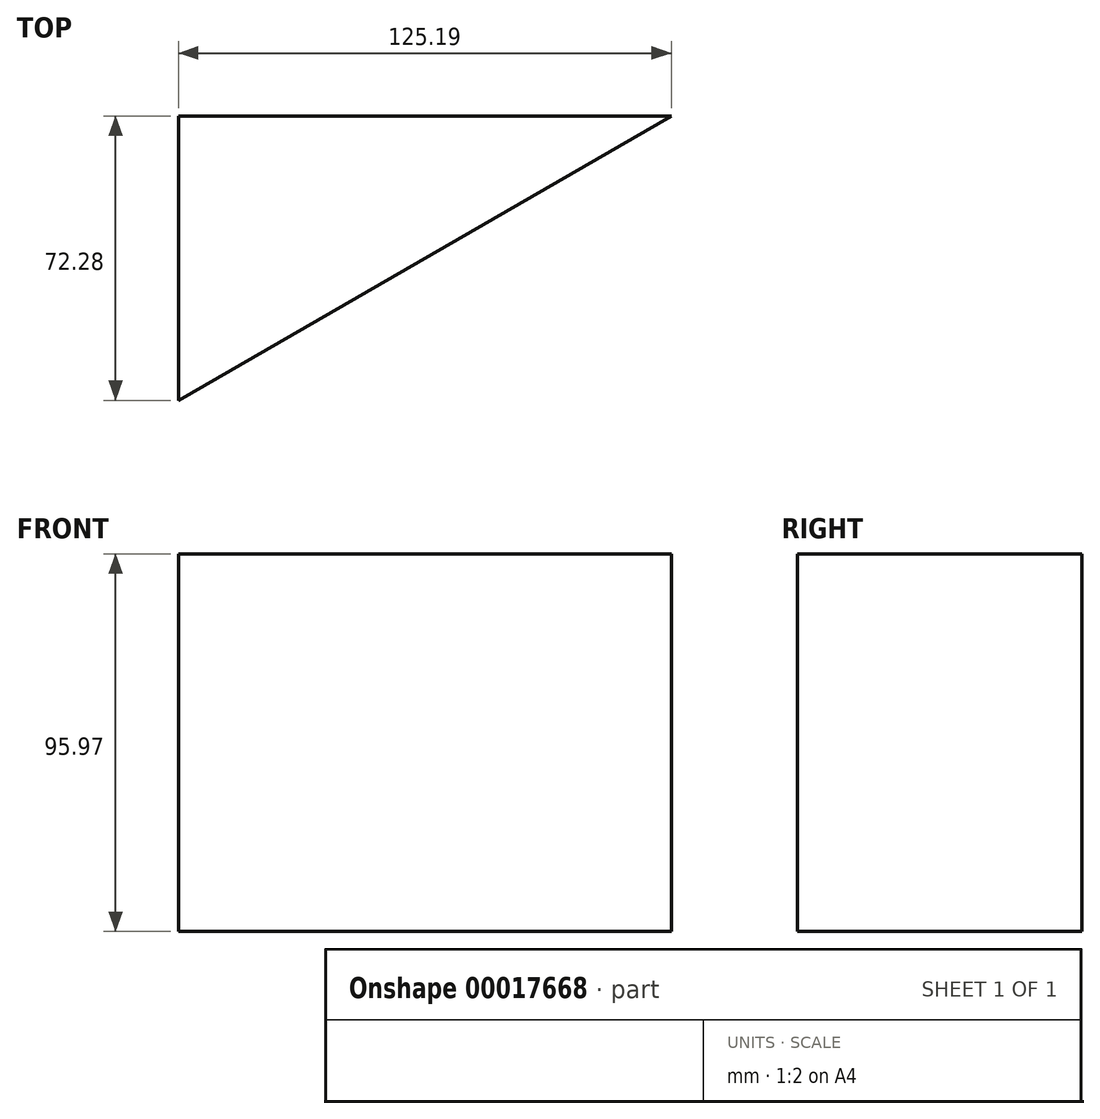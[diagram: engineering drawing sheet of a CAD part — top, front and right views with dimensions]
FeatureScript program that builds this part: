
annotation { "Feature Type Name" : "Feature", "Feature Type Description" : "" }
export const myFeature = defineFeature(function(context is Context, id is Id, definition is map)
    precondition{}
    {
        {
            var Q0;
            Q0=qCreatedBy(makeId("Top.planeOp"),FACE);
            var sketch = newSketch(context, id + "F0", { "sketchPlane" : qUnion([Q0])});
            skLineSegment(sketch, "E0", {"start": v(0, 0) * mm, "end": v(125.2, 72.28) * mm});
            skLineSegment(sketch, "E1", {"start": v(125.2, 72.28) * mm, "end": v(0, 72.28) * mm});
            skLineSegment(sketch, "E2", {"start": v(0, 72.28) * mm, "end": v(0, 0) * mm});
            skSolve(sketch);
        }
        {
            var Q0;
            Q0 = qSketchRegion(id + "F0", true);
            extrude(context, id + "F1", {"entities" : qUnion([Q0]), "depth" : 95.97 * mm});
        }
    });
